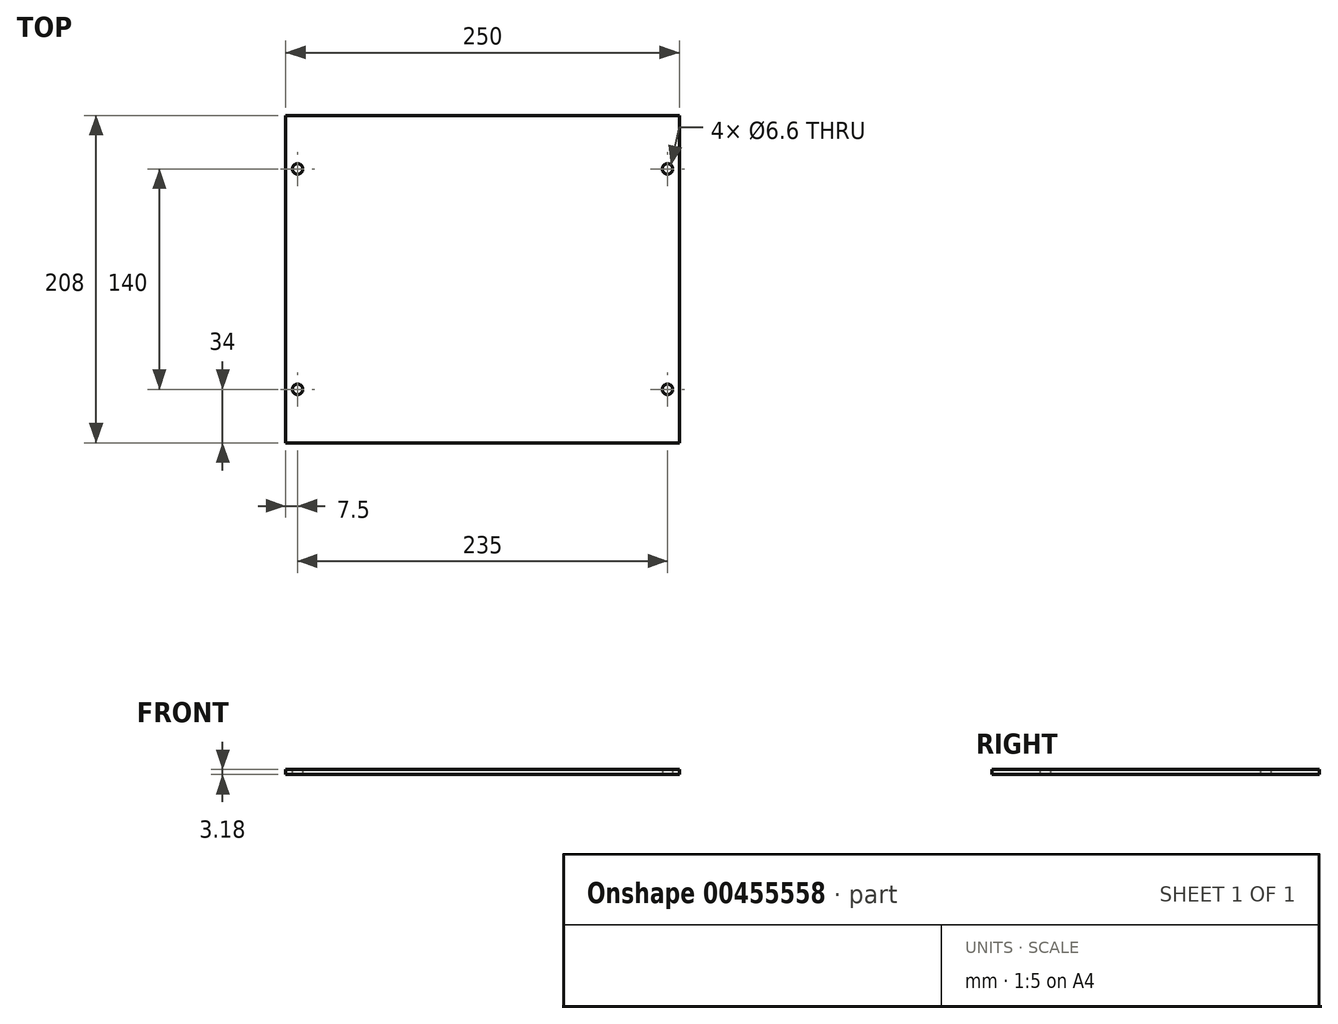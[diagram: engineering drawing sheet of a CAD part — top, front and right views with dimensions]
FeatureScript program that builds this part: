
annotation { "Feature Type Name" : "Feature", "Feature Type Description" : "" }
export const myFeature = defineFeature(function(context is Context, id is Id, definition is map)
    precondition{}
    {
        {
            var Q0;
            Q0=qCreatedBy(makeId("Top.planeOp"),FACE);
            var sketch = newSketch(context, id + "F0", { "sketchPlane" : qUnion([Q0])});
            skLineSegment(sketch, "E0.bottom", {"start": v(125, 104) * mm, "end": v(-125, 104) * mm});
            skLineSegment(sketch, "E0.top", {"start": v(125, -104) * mm, "end": v(-125, -104) * mm});
            skLineSegment(sketch, "E0.left", {"start": v(125, 104) * mm, "end": v(125, -104) * mm});
            skLineSegment(sketch, "E0.right", {"start": v(-125, 104) * mm, "end": v(-125, -104) * mm});
            skPoint(sketch, "E0.middle", {"position": v(0, 0) * mm});
            skCircle(sketch, "E1", {"center": v(117.5, -70) * mm, "radius": 3.3 * mm});
            skCircle(sketch, "E2.MirrorC", {"center": v(117.5, 70) * mm, "radius": 3.3 * mm});
            skCircle(sketch, "E3.MirrorC", {"center": v(-117.5, 70) * mm, "radius": 3.3 * mm});
            skCircle(sketch, "E4.MirrorC", {"center": v(-117.5, -70) * mm, "radius": 3.3 * mm});
            skSolve(sketch);
        }
        {
            var Q0;
            Q0=makeQuery(id+"F0.imprint","IMPRINT",FACE,{"disambiguationData":[TD([[makeQuery(id+"F0.imprint","IMPRINT",EDGE,{"derivedFrom":sQuery(id+"F0.wireOp",EDGE,"E0.bottom")}),1.0]])]});
            extrude(context, id + "F1", {"entities" : qUnion([Q0]), "depth" : 3.17 * mm});
        }
    });
